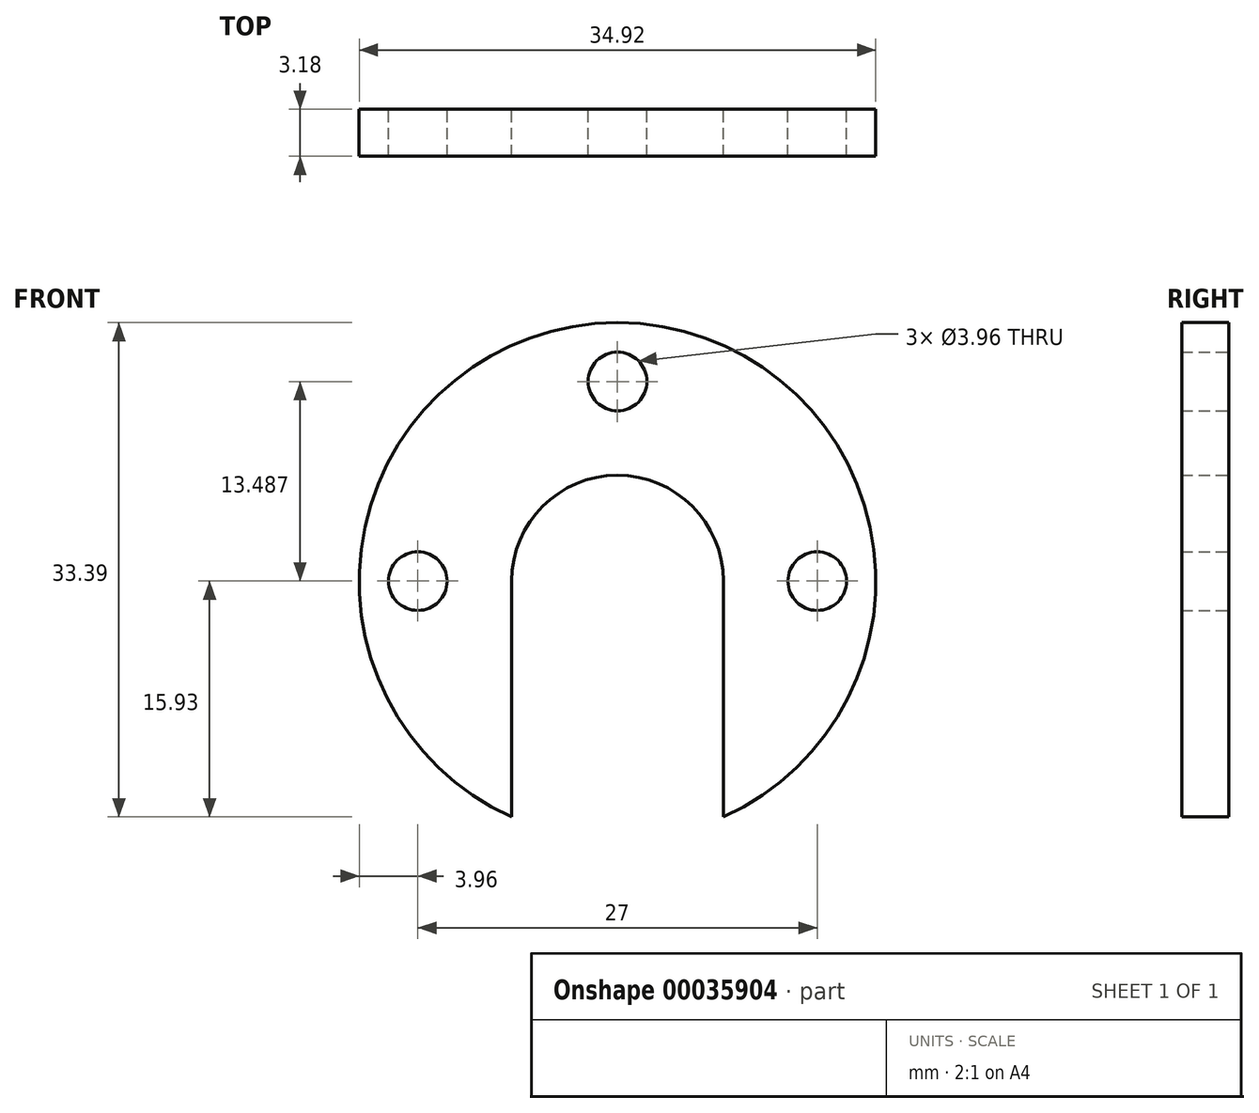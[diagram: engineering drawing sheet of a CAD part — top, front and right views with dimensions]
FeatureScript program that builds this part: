
annotation { "Feature Type Name" : "Feature", "Feature Type Description" : "" }
export const myFeature = defineFeature(function(context is Context, id is Id, definition is map)
    precondition{}
    {
        {
            var Q0;
            Q0=qCreatedBy(makeId("Front.planeOp"),FACE);
            var sketch = newSketch(context, id + "F0", { "sketchPlane" : qUnion([Q0])});
            skCircle(sketch, "E0", {"center": v(0, 0) * mm, "radius": 17.46 * mm});
            skCircle(sketch, "E1", {"center": v(0, 0) * mm, "radius": 7.15 * mm});
            skLineSegment(sketch, "E2", {"start": v(-7.15, 0) * mm, "end": v(-7.15, -15.93) * mm});
            skLineSegment(sketch, "E3", {"start": v(7.15, 0) * mm, "end": v(7.15, -15.93) * mm});
            skCircle(sketch, "E4", {"center": v(0, 13.49) * mm, "radius": 1.98 * mm});
            skCircle(sketch, "E5", {"center": v(-13.5, 0) * mm, "radius": 1.98 * mm});
            skCircle(sketch, "E6", {"center": v(13.5, 0) * mm, "radius": 1.98 * mm});
            skLineSegment(sketch, "E7", {"start": v(-13.5, 0) * mm, "end": v(13.5, 0) * mm, "construction": true});
            skSolve(sketch);
        }
        {
            var Q0;
            {var subQ1=sQuery(id+"F0.wireOp",EDGE,"E2");Q0=makeQuery(id+"F0.imprint","IMPRINT",FACE,{"disambiguationData":[TD([[makeQuery(id+"F0.imprint","IMPRINT",EDGE,{"derivedFrom":subQ1}),-1.0]])]});}
            extrude(context, id + "F1", {"entities" : qUnion([Q0]), "depth" : 3.17 * mm, "symmetric" : true});
        }
    });
